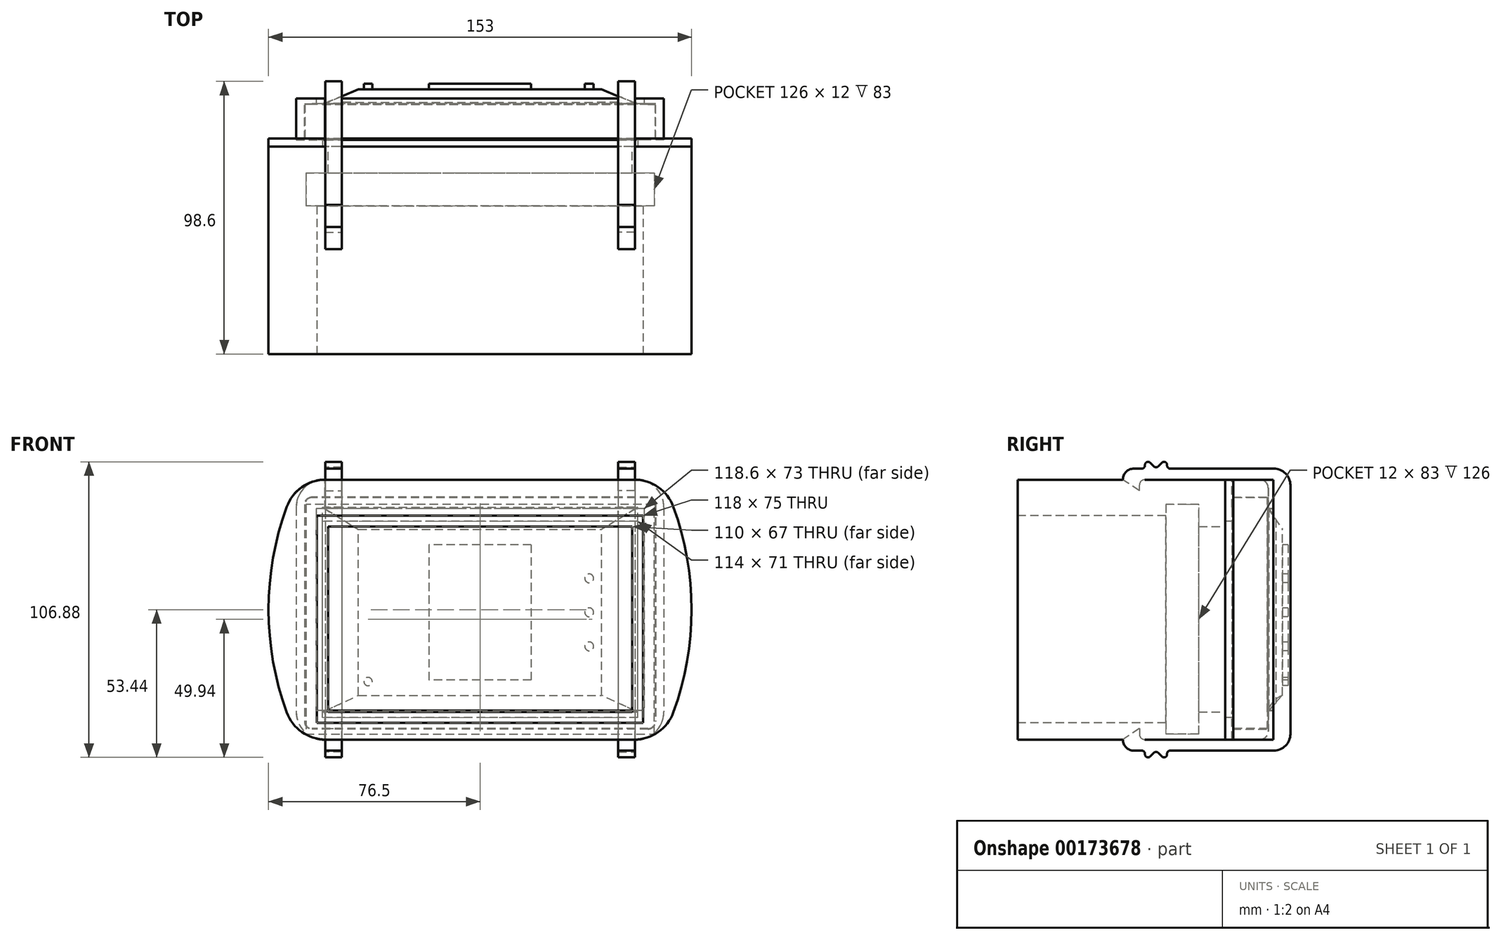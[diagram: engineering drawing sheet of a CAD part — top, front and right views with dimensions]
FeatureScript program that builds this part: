
annotation { "Feature Type Name" : "Feature", "Feature Type Description" : "" }
export const myFeature = defineFeature(function(context is Context, id is Id, definition is map)
    precondition{}
    {
        {
            var Q0;
            Q0=qCreatedBy(makeId("Front.planeOp"),FACE);
            var sketch = newSketch(context, id + "F0", { "sketchPlane" : qUnion([Q0])});
            skLineSegment(sketch, "E0.bottom", {"start": v(65.78, -47) * mm, "end": v(-65.78, -47) * mm});
            skLineSegment(sketch, "E0.top", {"start": v(65.78, 47) * mm, "end": v(-65.78, 47) * mm});
            skPoint(sketch, "E0.middle", {"position": v(0, 0) * mm});
            skArc(sketch, "E1", {"start": v(-65.78, 47) * mm, "mid": v(-76.5, 0) * mm, "end": v(-65.78, -47) * mm});
            skArc(sketch, "E2.MirrorCS", {"start": v(65.78, 47) * mm, "mid": v(76.5, 0) * mm, "end": v(65.78, -47) * mm});
            skLineSegment(sketch, "E3.bottom", {"start": v(55, -37) * mm, "end": v(-55, -37) * mm});
            skLineSegment(sketch, "E3.top", {"start": v(55, 30) * mm, "end": v(-55, 30) * mm});
            skLineSegment(sketch, "E3.left", {"start": v(55, -37) * mm, "end": v(55, 30) * mm});
            skLineSegment(sketch, "E3.right", {"start": v(-55, -37) * mm, "end": v(-55, 30) * mm});
            skPoint(sketch, "E3.middle", {"position": v(0, -3.5) * mm});
            skSolve(sketch);
        }
        {
            var Q0;
            Q0 = qSketchRegion(id + "F0", true);
            extrude(context, id + "F1", {"entities" : qUnion([Q0]), "depth" : 75 * mm});
        }
        {
            var Q0;
            Q0=qCreatedBy(makeId("Right.planeOp"),FACE);
            var sketch = newSketch(context, id + "F2", { "sketchPlane" : qUnion([Q0])});
            skLineSegment(sketch, "E4.0.1", {"start": v(-75, -41) * mm, "end": v(-75, -37) * mm});
            skLineSegment(sketch, "E4.0.3", {"start": v(-75, -37) * mm, "end": v(-75, -41) * mm});
            skLineSegment(sketch, "E5.0.1", {"start": v(-9.5, -37) * mm, "end": v(-75, -37) * mm});
            skLineSegment(sketch, "E5.0.3", {"start": v(-75, -37) * mm, "end": v(-9.5, -37) * mm});
            skLineSegment(sketch, "E6", {"start": v(-9.5, -37) * mm, "end": v(-9.5, -45) * mm});
            skLineSegment(sketch, "E7", {"start": v(-9.5, -45) * mm, "end": v(-21.5, -45) * mm});
            skLineSegment(sketch, "E8", {"start": v(-21.5, -45) * mm, "end": v(-21.5, -41) * mm});
            skLineSegment(sketch, "E9", {"start": v(-21.5, -41) * mm, "end": v(-75, -41) * mm});
            skPoint(sketch, "E10.orphan", {"position": v(-75, 47) * mm});
            skPoint(sketch, "E11.orphan", {"position": v(0, -37) * mm});
            skPoint(sketch, "E12.orphan", {"position": v(-75, -47) * mm});
            skSolve(sketch);
        }
        {
            var Q0;
            Q0 = qSketchRegion(id + "F2", true);
            var Q1;
            Q1=makeQuery(id+"F1.opExtrude","CAP_EDGE",EDGE,{"disambiguationData":[OSD([sQuery(id+"F0.wireOp",EDGE,"E3.bottom")])],"isStart":true});
            var Q2;
            Q2=makeQuery(id+"F1.opExtrude","CAP_EDGE",EDGE,{"disambiguationData":[OSD([sQuery(id+"F0.wireOp",EDGE,"E3.right")])],"isStart":true});
            var Q3;
            Q3=makeQuery(id+"F1.opExtrude","CAP_EDGE",EDGE,{"disambiguationData":[OSD([sQuery(id+"F0.wireOp",EDGE,"E3.top")])],"isStart":true});
            var Q4;
            Q4=makeQuery(id+"F1.opExtrude","CAP_EDGE",EDGE,{"disambiguationData":[OSD([sQuery(id+"F0.wireOp",EDGE,"E3.left")])],"isStart":true});
            sweep(context, id + "F3", {"operationType" : NewBodyOperationType.REMOVE, "profiles" : qUnion([Q0]), "path" : qUnion([Q1, Q2, Q3, Q4])});
        }
        {
            var Q0;
            Q0=makeQuery(id+"F1.opExtrude","SWEPT_EDGE",EDGE,{"disambiguationData":[OSD([sQuery(id+"F0.wireOp",EDGE,"E0.top"),sQuery(id+"F0.wireOp",EDGE,"E1")])]});
            var Q1;
            Q1=makeQuery(id+"F1.opExtrude","SWEPT_EDGE",EDGE,{"disambiguationData":[OSD([sQuery(id+"F0.wireOp",EDGE,"E0.top"),sQuery(id+"F0.wireOp",EDGE,"E2.MirrorCS")])]});
            var Q2;
            Q2=makeQuery(id+"F1.opExtrude","SWEPT_EDGE",EDGE,{"disambiguationData":[OSD([sQuery(id+"F0.wireOp",EDGE,"E0.bottom"),sQuery(id+"F0.wireOp",EDGE,"E2.MirrorCS")])]});
            var Q3;
            Q3=makeQuery(id+"F1.opExtrude","SWEPT_EDGE",EDGE,{"disambiguationData":[OSD([sQuery(id+"F0.wireOp",EDGE,"E0.bottom"),sQuery(id+"F0.wireOp",EDGE,"E1")])]});
            fillet(context, id + "F4", {"entities" : qUnion([Q0, Q1, Q2, Q3]), "radius" : 15 * mm, "tangentPropagation" : true, "allowEdgeOverflow" : false});
        }
        {
            var Q0;
            Q0=makeQuery(id+"F1.opExtrude","CAP_FACE",FACE,{"disambiguationData":[OSD([sQuery(id+"F0.wireOp",EDGE,"E0.bottom"),sQuery(id+"F0.wireOp",EDGE,"E0.top"),sQuery(id+"F0.wireOp",EDGE,"E1"),sQuery(id+"F0.wireOp",EDGE,"E2.MirrorCS"),sQuery(id+"F0.wireOp",EDGE,"E3.bottom"),sQuery(id+"F0.wireOp",EDGE,"E3.top"),sQuery(id+"F0.wireOp",EDGE,"E3.left"),sQuery(id+"F0.wireOp",EDGE,"E3.right")])],"isStart":true});
            var sketch = newSketch(context, id + "F5", { "sketchPlane" : qUnion([Q0])});
            skLineSegment(sketch, "E13.0", {"start": v(-55, 30) * mm, "end": v(55, 30) * mm});
            skLineSegment(sketch, "E14.0", {"start": v(-55, -37) * mm, "end": v(-55, 30) * mm});
            skLineSegment(sketch, "E15.0", {"start": v(-55, -37) * mm, "end": v(55, -37) * mm});
            skLineSegment(sketch, "E16.0", {"start": v(55, -37) * mm, "end": v(55, 30) * mm});
            skLineSegment(sketch, "E17.0", {"start": v(-55.85, 47) * mm, "end": v(55.85, 47) * mm});
            skArc(sketch, "E18.0", {"start": v(-55.85, 47) * mm, "mid": v(-64.44, 44.3) * mm, "end": v(-69.94, 37.14) * mm});
            skArc(sketch, "E19.0", {"start": v(-69.94, 37.14) * mm, "mid": v(-76.5, 0) * mm, "end": v(-69.94, -37.14) * mm});
            skArc(sketch, "E20.0", {"start": v(-69.94, -37.14) * mm, "mid": v(-64.44, -44.3) * mm, "end": v(-55.85, -47) * mm});
            skLineSegment(sketch, "E21.0", {"start": v(-55.85, -47) * mm, "end": v(55.85, -47) * mm});
            skArc(sketch, "E22.0", {"start": v(55.85, -47) * mm, "mid": v(64.44, -44.3) * mm, "end": v(69.94, -37.14) * mm});
            skArc(sketch, "E23.0", {"start": v(69.94, 37.14) * mm, "mid": v(76.5, 0) * mm, "end": v(69.94, -37.14) * mm});
            skArc(sketch, "E24.0", {"start": v(69.94, 37.14) * mm, "mid": v(64.44, 44.3) * mm, "end": v(55.85, 47) * mm});
            skLineSegment(sketch, "E25.0", {"start": v(-57, 32) * mm, "end": v(57, 32) * mm});
            skLineSegment(sketch, "E25.1", {"start": v(-57, -39) * mm, "end": v(-57, 32) * mm});
            skLineSegment(sketch, "E25.2", {"start": v(-57, -39) * mm, "end": v(57, -39) * mm});
            skLineSegment(sketch, "E25.3", {"start": v(57, -39) * mm, "end": v(57, 32) * mm});
            skSolve(sketch);
        }
        {
            var Q0;
            Q0=makeQuery(id+"F5.imprint","IMPRINT",FACE,{"disambiguationData":[TD([[makeQuery(id+"F5.imprint","IMPRINT",EDGE,{"derivedFrom":sQuery(id+"F5.wireOp",EDGE,"E17.0")}),-1.0]])]});
            extrude(context, id + "F6", {"entities" : qUnion([Q0]), "depth" : 3 * mm});
        }
        {
            var Q0;
            Q0=makeQuery(id+"F6.opExtrude","CAP_FACE",FACE,{"disambiguationData":[OSD([sQuery(id+"F5.wireOp",EDGE,"E17.0"),sQuery(id+"F5.wireOp",EDGE,"E18.0"),sQuery(id+"F5.wireOp",EDGE,"E19.0"),sQuery(id+"F5.wireOp",EDGE,"E20.0"),sQuery(id+"F5.wireOp",EDGE,"E21.0"),sQuery(id+"F5.wireOp",EDGE,"E22.0"),sQuery(id+"F5.wireOp",EDGE,"E23.0"),sQuery(id+"F5.wireOp",EDGE,"E24.0"),sQuery(id+"F5.wireOp",EDGE,"E25.0"),sQuery(id+"F5.wireOp",EDGE,"E25.1"),sQuery(id+"F5.wireOp",EDGE,"E25.2"),sQuery(id+"F5.wireOp",EDGE,"E25.3")])],"isStart":false});
            var sketch = newSketch(context, id + "F7", { "sketchPlane" : qUnion([Q0])});
            skLineSegment(sketch, "E26.bottom", {"start": v(-63.3, 40.5) * mm, "end": v(63.3, 40.5) * mm});
            skLineSegment(sketch, "E26.top", {"start": v(-63.3, -43) * mm, "end": v(63.3, -43) * mm});
            skLineSegment(sketch, "E26.left", {"start": v(-63.3, 40.5) * mm, "end": v(-63.3, -43) * mm});
            skLineSegment(sketch, "E26.right", {"start": v(63.3, 40.5) * mm, "end": v(63.3, -43) * mm});
            skPoint(sketch, "E26.middle", {"position": v(0, -1.25) * mm});
            skSolve(sketch);
        }
        {
            var Q0;
            Q0 = qSketchRegion(id + "F7", true);
            extrude(context, id + "F8", {"entities" : qUnion([Q0]), "depth" : 12.3 * mm});
        }
        {
            var Q0;
            Q0=makeQuery(id+"F8.opExtrude","CAP_FACE",FACE,{"disambiguationData":[OSD([sQuery(id+"F7.wireOp",EDGE,"E26.bottom"),sQuery(id+"F7.wireOp",EDGE,"E26.top"),sQuery(id+"F7.wireOp",EDGE,"E26.left"),sQuery(id+"F7.wireOp",EDGE,"E26.right")])],"isStart":false});
            var sketch = newSketch(context, id + "F9", { "sketchPlane" : qUnion([Q0])});
            skLineSegment(sketch, "E27.bottom", {"start": v(57, -37) * mm, "end": v(-57, -37) * mm});
            skLineSegment(sketch, "E27.top", {"start": v(57, 37) * mm, "end": v(-57, 37) * mm});
            skLineSegment(sketch, "E27.left", {"start": v(57, -37) * mm, "end": v(57, 37) * mm});
            skLineSegment(sketch, "E27.right", {"start": v(-57, -37) * mm, "end": v(-57, 37) * mm});
            skPoint(sketch, "E27.middle", {"position": v(0, 0) * mm});
            skSolve(sketch);
        }
        {
            var Q0;
            Q0=makeQuery(id+"F9.imprint","IMPRINT",FACE,{"disambiguationData":[TD([[makeQuery(id+"F9.imprint","IMPRINT",EDGE,{"derivedFrom":sQuery(id+"F9.wireOp",EDGE,"E27.bottom")}),1.0]])]});
            cPlane(context, id + "F10", {"entities" : qUnion([Q0]), "cplaneType" : CPlaneType.OFFSET, "offset" : 5.4 * mm, "width" : 150 * mm, "height" : 150 * mm});
        }
        {
            var Q0;
            Q0=qCreatedBy(id+"F10.planeOp",FACE);
            var sketch = newSketch(context, id + "F11", { "sketchPlane" : qUnion([Q0])});
            skLineSegment(sketch, "E28.bottom", {"start": v(44, -31) * mm, "end": v(-44, -31) * mm});
            skLineSegment(sketch, "E28.top", {"start": v(44, 29) * mm, "end": v(-44, 29) * mm});
            skLineSegment(sketch, "E28.left", {"start": v(44, -31) * mm, "end": v(44, 29) * mm});
            skLineSegment(sketch, "E28.right", {"start": v(-44, -31) * mm, "end": v(-44, 29) * mm});
            skPoint(sketch, "E28.middle", {"position": v(0, -1) * mm});
            skSolve(sketch);
        }
        {
            var Q0;
            Q0=qCreatedBy(makeId("Right.planeOp"),FACE);
            var sketch = newSketch(context, id + "F12", { "sketchPlane" : qUnion([Q0])});
            skArc(sketch, "E29", {"start": v(20.7, -31) * mm, "mid": v(17.32, -33.39) * mm, "end": v(15.3, -37) * mm});
            skSolve(sketch);
        }
        {
            var Q1;
            Q1=makeQuery(id+"F9.imprint","IMPRINT",FACE,{"disambiguationData":[TD([[makeQuery(id+"F9.imprint","IMPRINT",EDGE,{"derivedFrom":sQuery(id+"F9.wireOp",EDGE,"E27.bottom")}),-1.0]])]});
            var Q2;
            Q2=makeQuery(id+"F11.imprint","IMPRINT",FACE,{"disambiguationData":[TD([[makeQuery(id+"F11.imprint","IMPRINT",EDGE,{"derivedFrom":sQuery(id+"F11.wireOp",EDGE,"E28.bottom")}),-1.0]])]});
            var Q3;
            Q3=sQuery(id+"F12.wireOp",EDGE,"E29");
            loft(context, id + "F13", {"operationType" : NewBodyOperationType.ADD, "addGuides" : true, "sheetProfilesArray" : [{ "sheetProfileEntities" : qUnion([Q1]) }, { "sheetProfileEntities" : qUnion([Q2]) }], "guidesArray" : [{ "guideEntities" : qUnion([Q3]), "guideDerivativeType" : LoftGuideDerivativeType.DEFAULT, "guideDerivativeMagnitude" : 1 }]});
        }
        {
            var Q0;
            Q0=makeQuery(id+"F8.opExtrude","SWEPT_EDGE",EDGE,{"disambiguationData":[OSD([sQuery(id+"F7.wireOp",EDGE,"E26.bottom"),sQuery(id+"F7.wireOp",EDGE,"E26.left")])]});
            var Q1;
            Q1=makeQuery(id+"F8.opExtrude","SWEPT_EDGE",EDGE,{"disambiguationData":[OSD([sQuery(id+"F7.wireOp",EDGE,"E26.top"),sQuery(id+"F7.wireOp",EDGE,"E26.left")])]});
            var Q2;
            Q2=makeQuery(id+"F8.opExtrude","SWEPT_EDGE",EDGE,{"disambiguationData":[OSD([sQuery(id+"F7.wireOp",EDGE,"E26.bottom"),sQuery(id+"F7.wireOp",EDGE,"E26.right")])]});
            var Q3;
            Q3=makeQuery(id+"F8.opExtrude","SWEPT_EDGE",EDGE,{"disambiguationData":[OSD([sQuery(id+"F7.wireOp",EDGE,"E26.top"),sQuery(id+"F7.wireOp",EDGE,"E26.right")])]});
            fillet(context, id + "F14", {"entities" : qUnion([Q0, Q1, Q2, Q3]), "radius" : 2.5 * mm, "tangentPropagation" : true, "allowEdgeOverflow" : false});
        }
        {
            var Q0;
            Q0=makeQuery(id+"F13.opLoft","CAP_FACE",FACE,{"disambiguationData":[OSD([makeQuery(id+"F11.imprint","IMPRINT",FACE,{"disambiguationData":[TD([[makeQuery(id+"F11.imprint","IMPRINT",EDGE,{"derivedFrom":sQuery(id+"F11.wireOp",EDGE,"E28.bottom")}),-1.0]])]})])],"isStart":true});
            var sketch = newSketch(context, id + "F15", { "sketchPlane" : qUnion([Q0])});
            skCircle(sketch, "E30", {"center": v(-39.5, 11.3) * mm, "radius": 1.6 * mm});
            skLineSegment(sketch, "E31.bottom", {"start": v(-44, -1) * mm, "end": v(44, -1) * mm, "construction": true});
            skLineSegment(sketch, "E31.top", {"start": v(-44, -1) * mm, "end": v(44, -1) * mm, "construction": true});
            skLineSegment(sketch, "E31.left", {"start": v(-44, -1) * mm, "end": v(-44, -1) * mm});
            skLineSegment(sketch, "E31.right", {"start": v(44, -1) * mm, "end": v(44, -1) * mm});
            skCircle(sketch, "E32", {"center": v(-39.5, -1) * mm, "radius": 1.6 * mm});
            skCircle(sketch, "E33.MirrorC", {"center": v(-39.5, -13.3) * mm, "radius": 1.6 * mm});
            skCircle(sketch, "E34", {"center": v(40.5, -26) * mm, "radius": 1.5 * mm});
            skLineSegment(sketch, "E35.bottom", {"start": v(-18.5, 23.5) * mm, "end": v(18.5, 23.5) * mm});
            skLineSegment(sketch, "E35.top", {"start": v(-18.5, -25.5) * mm, "end": v(18.5, -25.5) * mm});
            skLineSegment(sketch, "E35.left", {"start": v(-18.5, 23.5) * mm, "end": v(-18.5, -25.5) * mm});
            skLineSegment(sketch, "E35.right", {"start": v(18.5, 23.5) * mm, "end": v(18.5, -25.5) * mm});
            skPoint(sketch, "E35.middle", {"position": v(0, -1) * mm});
            skSolve(sketch);
        }
        {
            var Q0;
            Q0 = qSketchRegion(id + "F15", true);
            extrude(context, id + "F16", {"entities" : qUnion([Q0]), "operationType" : NewBodyOperationType.ADD, "depth" : 2 * mm});
        }
        {
            var Q0;
            Q0=makeQuery(id+"F6.opExtrude","CAP_FACE",FACE,{"disambiguationData":[OSD([sQuery(id+"F5.wireOp",EDGE,"E17.0"),sQuery(id+"F5.wireOp",EDGE,"E18.0"),sQuery(id+"F5.wireOp",EDGE,"E19.0"),sQuery(id+"F5.wireOp",EDGE,"E20.0"),sQuery(id+"F5.wireOp",EDGE,"E21.0"),sQuery(id+"F5.wireOp",EDGE,"E22.0"),sQuery(id+"F5.wireOp",EDGE,"E23.0"),sQuery(id+"F5.wireOp",EDGE,"E24.0"),sQuery(id+"F5.wireOp",EDGE,"E25.0"),sQuery(id+"F5.wireOp",EDGE,"E25.1"),sQuery(id+"F5.wireOp",EDGE,"E25.2"),sQuery(id+"F5.wireOp",EDGE,"E25.3")])],"isStart":false});
            var sketch = newSketch(context, id + "F17", { "sketchPlane" : qUnion([Q0])});
            skLineSegment(sketch, "E36.bottom", {"start": v(-66.5, 47) * mm, "end": v(66.5, 47) * mm});
            skLineSegment(sketch, "E36.top", {"start": v(-66.5, -47) * mm, "end": v(66.5, -47) * mm});
            skLineSegment(sketch, "E36.left", {"start": v(-66.5, 47) * mm, "end": v(-66.5, -47) * mm});
            skLineSegment(sketch, "E36.right", {"start": v(66.5, 47) * mm, "end": v(66.5, -47) * mm});
            skPoint(sketch, "E36.middle", {"position": v(0, 0) * mm});
            skLineSegment(sketch, "E37.bottom", {"start": v(-59.3, 36.5) * mm, "end": v(59.3, 36.5) * mm});
            skLineSegment(sketch, "E37.top", {"start": v(-59.3, -36.5) * mm, "end": v(59.3, -36.5) * mm});
            skLineSegment(sketch, "E37.left", {"start": v(-59.3, 36.5) * mm, "end": v(-59.3, -36.5) * mm});
            skLineSegment(sketch, "E37.right", {"start": v(59.3, 36.5) * mm, "end": v(59.3, -36.5) * mm});
            skSolve(sketch);
        }
        {
            var Q0;
            Q0 = qSketchRegion(id + "F17", true);
            extrude(context, id + "F18", {"entities" : qUnion([Q0]), "depth" : 15 * mm});
        }
        {
            var Q0;
            Q0=makeQuery(id+"F18.opExtrude","SWEPT_EDGE",EDGE,{"disambiguationData":[OSD([sQuery(id+"F17.wireOp",EDGE,"E36.bottom"),sQuery(id+"F17.wireOp",EDGE,"E36.left")])]});
            var Q1;
            Q1=makeQuery(id+"F18.opExtrude","SWEPT_EDGE",EDGE,{"disambiguationData":[OSD([sQuery(id+"F17.wireOp",EDGE,"E36.top"),sQuery(id+"F17.wireOp",EDGE,"E36.left")])]});
            var Q2;
            Q2=makeQuery(id+"F18.opExtrude","SWEPT_EDGE",EDGE,{"disambiguationData":[OSD([sQuery(id+"F17.wireOp",EDGE,"E36.bottom"),sQuery(id+"F17.wireOp",EDGE,"E36.right")])]});
            var Q3;
            Q3=makeQuery(id+"F18.opExtrude","SWEPT_EDGE",EDGE,{"disambiguationData":[OSD([sQuery(id+"F17.wireOp",EDGE,"E36.top"),sQuery(id+"F17.wireOp",EDGE,"E36.right")])]});
            fillet(context, id + "F19", {"entities" : qUnion([Q0, Q1, Q2, Q3]), "radius" : 10 * mm, "tangentPropagation" : true, "allowEdgeOverflow" : false});
        }
        {
            var Q0;
            Q0=makeQuery(id+"F18.opExtrude","SWEPT_BODY",BODY,{"disambiguationData":[OSD([sQuery(id+"F17.wireOp",EDGE,"E36.bottom"),sQuery(id+"F17.wireOp",EDGE,"E36.top"),sQuery(id+"F17.wireOp",EDGE,"E36.left"),sQuery(id+"F17.wireOp",EDGE,"E36.right"),sQuery(id+"F17.wireOp",EDGE,"E37.bottom"),sQuery(id+"F17.wireOp",EDGE,"E37.top"),sQuery(id+"F17.wireOp",EDGE,"E37.left"),sQuery(id+"F17.wireOp",EDGE,"E37.right")])]});
            var Q1;
            {var subQ0=sQuery(id+"F0.wireOp",EDGE,"E0.top");Q1=makeQuery(id+"F4.opFillet","BLEND_EDGE",EDGE,{"blendedFrom":[makeQuery(id+"F1.opExtrude","SWEPT_EDGE",EDGE,{"disambiguationData":[OSD([subQ0,sQuery(id+"F0.wireOp",EDGE,"E2.MirrorCS")])]}),makeQuery(id+"F1.opExtrude","SWEPT_FACE",FACE,{"disambiguationData":[OSD([subQ0])]})],"blendedInto":[makeQuery(id+"F1.opExtrude","SWEPT_FACE",FACE,{"disambiguationData":[OSD([subQ0])]})]});}
            transform(context, id + "F20", {"entities" : qUnion([Q0]), "transformType" : TransformType.TRANSLATION_DISTANCE, "transformDirection" : qUnion([Q1]), "distance" : 0.6 * mm, "oppositeDirection" : true, "makeCopy" : false});
        }
        {
            var Q0;
            Q0=makeQuery(id+"F8.opExtrude","SWEPT_BODY",BODY,{"disambiguationData":[OSD([sQuery(id+"F7.wireOp",EDGE,"E26.bottom"),sQuery(id+"F7.wireOp",EDGE,"E26.top"),sQuery(id+"F7.wireOp",EDGE,"E26.left"),sQuery(id+"F7.wireOp",EDGE,"E26.right")])]});
            var Q1;
            Q1=makeQuery(id+"F18.opExtrude","SWEPT_BODY",BODY,{"disambiguationData":[OSD([sQuery(id+"F17.wireOp",EDGE,"E36.bottom"),sQuery(id+"F17.wireOp",EDGE,"E36.top"),sQuery(id+"F17.wireOp",EDGE,"E36.left"),sQuery(id+"F17.wireOp",EDGE,"E36.right"),sQuery(id+"F17.wireOp",EDGE,"E37.bottom"),sQuery(id+"F17.wireOp",EDGE,"E37.top"),sQuery(id+"F17.wireOp",EDGE,"E37.left"),sQuery(id+"F17.wireOp",EDGE,"E37.right")])]});
            booleanBodies(context, id + "F21", {"operationType" : BooleanOperationType.SUBTRACTION, "tools" : qUnion([Q0]), "targets" : qUnion([Q1]), "offset" : true, "offsetAll" : true, "offsetDistance" : 0.2 * mm, "keepTools" : true});
        }
        {
            var Q0;
            Q0=qCreatedBy(makeId("Right.planeOp"),FACE);
            var sketch = newSketch(context, id + "F22", { "sketchPlane" : qUnion([Q0])});
            skLineSegment(sketch, "E38", {"start": v(-28, 43) * mm, "end": v(-34, 47) * mm});
            skLineSegment(sketch, "E39", {"start": v(-34, 47) * mm, "end": v(-34, 51) * mm});
            skLineSegment(sketch, "E40", {"start": v(-34, 51) * mm, "end": v(-26, 51) * mm});
            skLineSegment(sketch, "E41", {"start": v(-28, 43) * mm, "end": v(-28, 47) * mm});
            skLineSegment(sketch, "E42", {"start": v(-28, 47) * mm, "end": v(18.6, 47) * mm});
            skLineSegment(sketch, "E43.MirrorCS", {"start": v(-34, -51) * mm, "end": v(-26, -51) * mm});
            skLineSegment(sketch, "E44.MirrorCS", {"start": v(-28, -47) * mm, "end": v(18.6, -47) * mm});
            skLineSegment(sketch, "E45.MirrorCS", {"start": v(-28, -43) * mm, "end": v(-28, -47) * mm});
            skLineSegment(sketch, "E46.MirrorCS", {"start": v(-28, -43) * mm, "end": v(-34, -47) * mm});
            skLineSegment(sketch, "E47.MirrorCS", {"start": v(-34, -47) * mm, "end": v(-34, -51) * mm});
            skLineSegment(sketch, "E48", {"start": v(18.6, 47) * mm, "end": v(18.6, -47) * mm});
            skLineSegment(sketch, "E49", {"start": v(26.6, 51) * mm, "end": v(26.6, -51) * mm});
            skLineSegment(sketch, "E50", {"start": v(-26, -51) * mm, "end": v(-26, -55) * mm});
            skLineSegment(sketch, "E51", {"start": v(-26, -55) * mm, "end": v(-22, -51) * mm});
            skLineSegment(sketch, "E52", {"start": v(-22, -51) * mm, "end": v(-18, -55) * mm});
            skLineSegment(sketch, "E53", {"start": v(-18, -55) * mm, "end": v(-18, -51) * mm});
            skLineSegment(sketch, "E54.trimOffspring", {"start": v(-18, -51) * mm, "end": v(26.6, -51) * mm});
            skLineSegment(sketch, "E55.MirrorCS", {"start": v(-26, 51) * mm, "end": v(-26, 55) * mm});
            skLineSegment(sketch, "E56.MirrorCS", {"start": v(-26, 55) * mm, "end": v(-22, 51) * mm});
            skLineSegment(sketch, "E57.MirrorCS", {"start": v(-22, 51) * mm, "end": v(-18, 55) * mm});
            skLineSegment(sketch, "E58.MirrorCS", {"start": v(-18, 55) * mm, "end": v(-18, 51) * mm});
            skLineSegment(sketch, "E59.trimOffspring", {"start": v(-18, 51) * mm, "end": v(26.6, 51) * mm});
            skSolve(sketch);
        }
        {
            var Q0;
            Q0 = qSketchRegion(id + "F22", true);
            extrude(context, id + "F23", {"entities" : qUnion([Q0]), "depth" : 6 * mm});
        }
        {
            var Q0;
            Q0=makeQuery(id+"F23.opExtrude","SWEPT_EDGE",EDGE,{"disambiguationData":[OSD([sQuery(id+"F22.wireOp",EDGE,"E49"),sQuery(id+"F22.wireOp",EDGE,"E59.trimOffspring")])]});
            var Q1;
            Q1=makeQuery(id+"F23.opExtrude","SWEPT_EDGE",EDGE,{"disambiguationData":[OSD([sQuery(id+"F22.wireOp",EDGE,"E49"),sQuery(id+"F22.wireOp",EDGE,"E54.trimOffspring")])]});
            fillet(context, id + "F24", {"entities" : qUnion([Q0, Q1]), "radius" : 6 * mm, "tangentPropagation" : true, "allowEdgeOverflow" : false});
        }
        {
            var Q0;
            Q0=makeQuery(id+"F23.opExtrude","SWEPT_EDGE",EDGE,{"disambiguationData":[OSD([sQuery(id+"F22.wireOp",EDGE,"E42"),sQuery(id+"F22.wireOp",EDGE,"E48")])]});
            var Q1;
            Q1=makeQuery(id+"F23.opExtrude","SWEPT_EDGE",EDGE,{"disambiguationData":[OSD([sQuery(id+"F22.wireOp",EDGE,"E44.MirrorCS"),sQuery(id+"F22.wireOp",EDGE,"E48")])]});
            fillet(context, id + "F25", {"entities" : qUnion([Q0, Q1]), "radius" : 3 * mm, "tangentPropagation" : true, "allowEdgeOverflow" : false});
        }
        {
            var Q0;
            Q0=makeQuery(id+"F23.opExtrude","SWEPT_EDGE",EDGE,{"disambiguationData":[OSD([sQuery(id+"F22.wireOp",EDGE,"E41"),sQuery(id+"F22.wireOp",EDGE,"E42")])]});
            var Q1;
            Q1=makeQuery(id+"F23.opExtrude","SWEPT_EDGE",EDGE,{"disambiguationData":[OSD([sQuery(id+"F22.wireOp",EDGE,"E44.MirrorCS"),sQuery(id+"F22.wireOp",EDGE,"E45.MirrorCS")])]});
            fillet(context, id + "F26", {"entities" : qUnion([Q0, Q1]), "radius" : 2 * mm, "tangentPropagation" : true, "allowEdgeOverflow" : false});
        }
        {
            var Q0;
            Q0=makeQuery(id+"F23.opExtrude","SWEPT_EDGE",EDGE,{"disambiguationData":[OSD([sQuery(id+"F22.wireOp",EDGE,"E40"),sQuery(id+"F22.wireOp",EDGE,"E55.MirrorCS")])]});
            var Q1;
            Q1=makeQuery(id+"F23.opExtrude","SWEPT_EDGE",EDGE,{"disambiguationData":[OSD([sQuery(id+"F22.wireOp",EDGE,"E58.MirrorCS"),sQuery(id+"F22.wireOp",EDGE,"E59.trimOffspring")])]});
            var Q2;
            Q2=makeQuery(id+"F23.opExtrude","SWEPT_EDGE",EDGE,{"disambiguationData":[OSD([sQuery(id+"F22.wireOp",EDGE,"E56.MirrorCS"),sQuery(id+"F22.wireOp",EDGE,"E57.MirrorCS")])]});
            var Q3;
            Q3=makeQuery(id+"F23.opExtrude","SWEPT_EDGE",EDGE,{"disambiguationData":[OSD([sQuery(id+"F22.wireOp",EDGE,"E57.MirrorCS"),sQuery(id+"F22.wireOp",EDGE,"E58.MirrorCS")])]});
            var Q4;
            Q4=makeQuery(id+"F23.opExtrude","SWEPT_EDGE",EDGE,{"disambiguationData":[OSD([sQuery(id+"F22.wireOp",EDGE,"E55.MirrorCS"),sQuery(id+"F22.wireOp",EDGE,"E56.MirrorCS")])]});
            var Q5;
            Q5=makeQuery(id+"F23.opExtrude","SWEPT_EDGE",EDGE,{"disambiguationData":[OSD([sQuery(id+"F22.wireOp",EDGE,"E43.MirrorCS"),sQuery(id+"F22.wireOp",EDGE,"E50")])]});
            var Q6;
            Q6=makeQuery(id+"F23.opExtrude","SWEPT_EDGE",EDGE,{"disambiguationData":[OSD([sQuery(id+"F22.wireOp",EDGE,"E50"),sQuery(id+"F22.wireOp",EDGE,"E51")])]});
            var Q7;
            Q7=makeQuery(id+"F23.opExtrude","SWEPT_EDGE",EDGE,{"disambiguationData":[OSD([sQuery(id+"F22.wireOp",EDGE,"E51"),sQuery(id+"F22.wireOp",EDGE,"E52")])]});
            var Q8;
            Q8=makeQuery(id+"F23.opExtrude","SWEPT_EDGE",EDGE,{"disambiguationData":[OSD([sQuery(id+"F22.wireOp",EDGE,"E52"),sQuery(id+"F22.wireOp",EDGE,"E53")])]});
            var Q9;
            Q9=makeQuery(id+"F23.opExtrude","SWEPT_EDGE",EDGE,{"disambiguationData":[OSD([sQuery(id+"F22.wireOp",EDGE,"E53"),sQuery(id+"F22.wireOp",EDGE,"E54.trimOffspring")])]});
            fillet(context, id + "F27", {"entities" : qUnion([Q0, Q1, Q2, Q3, Q4, Q5, Q6, Q7, Q8, Q9]), "radius" : 1.1 * mm, "tangentPropagation" : true, "allowEdgeOverflow" : false});
        }
        {
            var Q0;
            Q0=makeQuery(id+"F23.opExtrude","SWEPT_EDGE",EDGE,{"disambiguationData":[OSD([sQuery(id+"F22.wireOp",EDGE,"E43.MirrorCS"),sQuery(id+"F22.wireOp",EDGE,"E47.MirrorCS")])]});
            var Q1;
            Q1=makeQuery(id+"F23.opExtrude","SWEPT_EDGE",EDGE,{"disambiguationData":[OSD([sQuery(id+"F22.wireOp",EDGE,"E39"),sQuery(id+"F22.wireOp",EDGE,"E40")])]});
            fillet(context, id + "F28", {"entities" : qUnion([Q0, Q1]), "radius" : 4 * mm, "tangentPropagation" : true, "allowEdgeOverflow" : false});
        }
        {
            var Q0;
            Q0=makeQuery(id+"F23.opExtrude","SWEPT_BODY",BODY,{"disambiguationData":[OSD([sQuery(id+"F22.wireOp",EDGE,"E38"),sQuery(id+"F22.wireOp",EDGE,"E39"),sQuery(id+"F22.wireOp",EDGE,"E40"),sQuery(id+"F22.wireOp",EDGE,"E41"),sQuery(id+"F22.wireOp",EDGE,"E42"),sQuery(id+"F22.wireOp",EDGE,"E43.MirrorCS"),sQuery(id+"F22.wireOp",EDGE,"E44.MirrorCS"),sQuery(id+"F22.wireOp",EDGE,"E45.MirrorCS"),sQuery(id+"F22.wireOp",EDGE,"E46.MirrorCS"),sQuery(id+"F22.wireOp",EDGE,"E47.MirrorCS"),sQuery(id+"F22.wireOp",EDGE,"E48"),sQuery(id+"F22.wireOp",EDGE,"E49")])]});
            var Q1;
            Q1=makeQuery(id+"F13.opLoft","MID_CAP_EDGE",EDGE,{"disambiguationData":[OSD([sQuery(id+"F11.wireOp",EDGE,"E28.top"),sQuery(id+"F11.wireOp",EDGE,"E28.left"),sQuery(id+"F11.wireOp",EDGE,"E28.right")])],"capPos":1.0});
            var Q2;
            Q2=makeQuery(id+"F13.opLoft","MID_CAP_EDGE",EDGE,{"disambiguationData":[OSD([sQuery(id+"F11.wireOp",EDGE,"E28.top"),sQuery(id+"F11.wireOp",EDGE,"E28.left"),sQuery(id+"F11.wireOp",EDGE,"E28.right")])],"capPos":1.0});
            transform(context, id + "F29", {"entities" : qUnion([Q0]), "transformType" : TransformType.TRANSLATION_3D, "dx" : 50 * mm, "dy" : -3 * mm, "dz" : 0 * mm, "makeCopy" : false});
        }
        {
            var Q0;
            Q0=makeQuery(id+"F23.opExtrude","SWEPT_BODY",BODY,{"disambiguationData":[OSD([sQuery(id+"F22.wireOp",EDGE,"E38"),sQuery(id+"F22.wireOp",EDGE,"E39"),sQuery(id+"F22.wireOp",EDGE,"E40"),sQuery(id+"F22.wireOp",EDGE,"E41"),sQuery(id+"F22.wireOp",EDGE,"E42"),sQuery(id+"F22.wireOp",EDGE,"E43.MirrorCS"),sQuery(id+"F22.wireOp",EDGE,"E44.MirrorCS"),sQuery(id+"F22.wireOp",EDGE,"E45.MirrorCS"),sQuery(id+"F22.wireOp",EDGE,"E46.MirrorCS"),sQuery(id+"F22.wireOp",EDGE,"E47.MirrorCS"),sQuery(id+"F22.wireOp",EDGE,"E48"),sQuery(id+"F22.wireOp",EDGE,"E49")])]});
            var Q1;
            Q1=qCreatedBy(makeId("Right.planeOp"),FACE);
            mirror(context, id + "F30", {"entities" : qUnion([Q0]), "mirrorPlane" : qUnion([Q1])});
        }
        {
            var Q0;
            Q0=makeQuery(id+"F8.opExtrude","SWEPT_BODY",BODY,{"disambiguationData":[OSD([sQuery(id+"F7.wireOp",EDGE,"E26.bottom"),sQuery(id+"F7.wireOp",EDGE,"E26.top"),sQuery(id+"F7.wireOp",EDGE,"E26.left"),sQuery(id+"F7.wireOp",EDGE,"E26.right")])]});
            var Q1;
            Q1=makeQuery(id+"F23.opExtrude","SWEPT_BODY",BODY,{"disambiguationData":[OSD([sQuery(id+"F22.wireOp",EDGE,"E38"),sQuery(id+"F22.wireOp",EDGE,"E39"),sQuery(id+"F22.wireOp",EDGE,"E40"),sQuery(id+"F22.wireOp",EDGE,"E41"),sQuery(id+"F22.wireOp",EDGE,"E42"),sQuery(id+"F22.wireOp",EDGE,"E43.MirrorCS"),sQuery(id+"F22.wireOp",EDGE,"E44.MirrorCS"),sQuery(id+"F22.wireOp",EDGE,"E45.MirrorCS"),sQuery(id+"F22.wireOp",EDGE,"E46.MirrorCS"),sQuery(id+"F22.wireOp",EDGE,"E47.MirrorCS"),sQuery(id+"F22.wireOp",EDGE,"E48"),sQuery(id+"F22.wireOp",EDGE,"E49")])]});
            var Q2;
            Q2=makeQuery(id+"F30.opPattern","COPY",BODY,{"derivedFrom":makeQuery(id+"F23.opExtrude","SWEPT_BODY",BODY,{"disambiguationData":[OSD([sQuery(id+"F22.wireOp",EDGE,"E38"),sQuery(id+"F22.wireOp",EDGE,"E39"),sQuery(id+"F22.wireOp",EDGE,"E40"),sQuery(id+"F22.wireOp",EDGE,"E41"),sQuery(id+"F22.wireOp",EDGE,"E42"),sQuery(id+"F22.wireOp",EDGE,"E43.MirrorCS"),sQuery(id+"F22.wireOp",EDGE,"E44.MirrorCS"),sQuery(id+"F22.wireOp",EDGE,"E45.MirrorCS"),sQuery(id+"F22.wireOp",EDGE,"E46.MirrorCS"),sQuery(id+"F22.wireOp",EDGE,"E47.MirrorCS"),sQuery(id+"F22.wireOp",EDGE,"E48"),sQuery(id+"F22.wireOp",EDGE,"E49")])]}),"instanceName":"1"});
            booleanBodies(context, id + "F31", {"operationType" : BooleanOperationType.SUBTRACTION, "tools" : qUnion([Q0]), "targets" : qUnion([Q1, Q2]), "offset" : true, "offsetAll" : true, "offsetDistance" : 0.1 * mm, "keepTools" : true});
        }
        {
            var Q0;
            Q0=makeQuery(id+"F23.opExtrude","SWEPT_BODY",BODY,{"disambiguationData":[OSD([sQuery(id+"F22.wireOp",EDGE,"E38"),sQuery(id+"F22.wireOp",EDGE,"E39"),sQuery(id+"F22.wireOp",EDGE,"E40"),sQuery(id+"F22.wireOp",EDGE,"E41"),sQuery(id+"F22.wireOp",EDGE,"E42"),sQuery(id+"F22.wireOp",EDGE,"E43.MirrorCS"),sQuery(id+"F22.wireOp",EDGE,"E44.MirrorCS"),sQuery(id+"F22.wireOp",EDGE,"E45.MirrorCS"),sQuery(id+"F22.wireOp",EDGE,"E46.MirrorCS"),sQuery(id+"F22.wireOp",EDGE,"E47.MirrorCS"),sQuery(id+"F22.wireOp",EDGE,"E48"),sQuery(id+"F22.wireOp",EDGE,"E49")])]});
            var Q1;
            Q1=makeQuery(id+"F30.opPattern","COPY",BODY,{"derivedFrom":makeQuery(id+"F23.opExtrude","SWEPT_BODY",BODY,{"disambiguationData":[OSD([sQuery(id+"F22.wireOp",EDGE,"E38"),sQuery(id+"F22.wireOp",EDGE,"E39"),sQuery(id+"F22.wireOp",EDGE,"E40"),sQuery(id+"F22.wireOp",EDGE,"E41"),sQuery(id+"F22.wireOp",EDGE,"E42"),sQuery(id+"F22.wireOp",EDGE,"E43.MirrorCS"),sQuery(id+"F22.wireOp",EDGE,"E44.MirrorCS"),sQuery(id+"F22.wireOp",EDGE,"E45.MirrorCS"),sQuery(id+"F22.wireOp",EDGE,"E46.MirrorCS"),sQuery(id+"F22.wireOp",EDGE,"E47.MirrorCS"),sQuery(id+"F22.wireOp",EDGE,"E48"),sQuery(id+"F22.wireOp",EDGE,"E49")])]}),"instanceName":"1"});
            var Q2;
            Q2=makeQuery(id+"F18.opExtrude","SWEPT_BODY",BODY,{"disambiguationData":[OSD([sQuery(id+"F17.wireOp",EDGE,"E36.bottom"),sQuery(id+"F17.wireOp",EDGE,"E36.top"),sQuery(id+"F17.wireOp",EDGE,"E36.left"),sQuery(id+"F17.wireOp",EDGE,"E36.right"),sQuery(id+"F17.wireOp",EDGE,"E37.bottom"),sQuery(id+"F17.wireOp",EDGE,"E37.top"),sQuery(id+"F17.wireOp",EDGE,"E37.left"),sQuery(id+"F17.wireOp",EDGE,"E37.right")])]});
            booleanBodies(context, id + "F32", {"operationType" : BooleanOperationType.SUBTRACTION, "tools" : qUnion([Q0, Q1]), "targets" : qUnion([Q2]), "offset" : true, "offsetAll" : true, "offsetDistance" : 0.05 * mm, "keepTools" : true});
        }
    });
